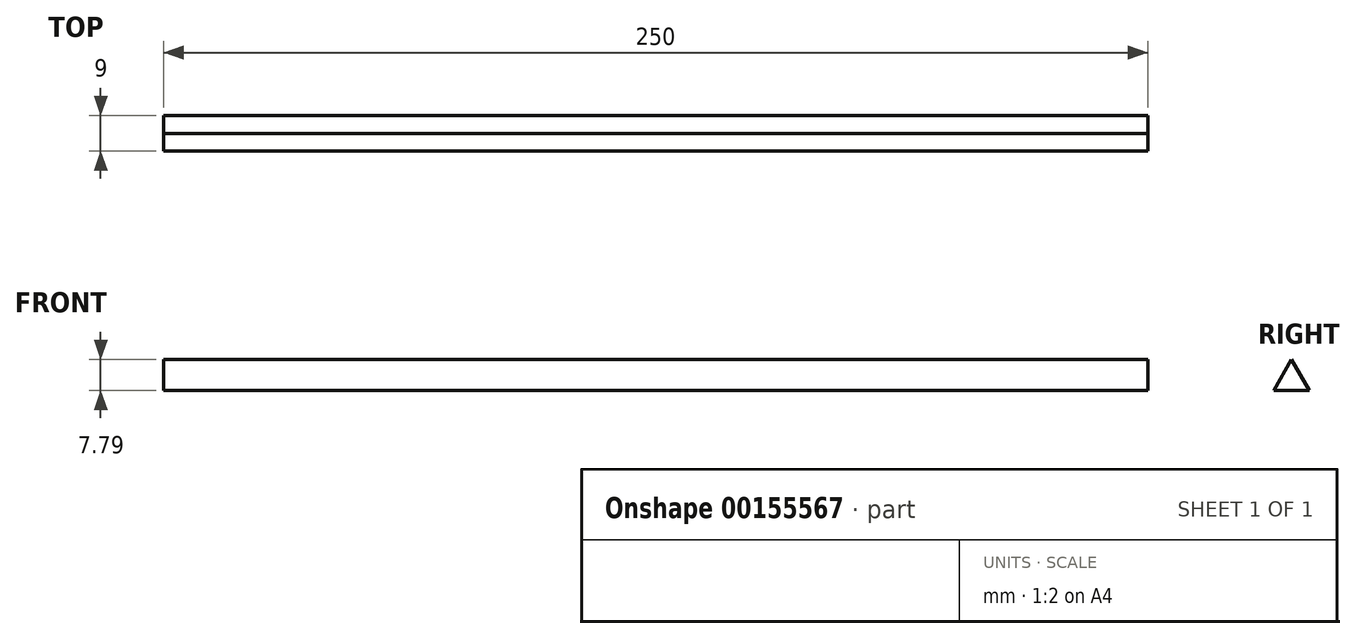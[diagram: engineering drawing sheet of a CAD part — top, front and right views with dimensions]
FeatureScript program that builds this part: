
annotation { "Feature Type Name" : "Feature", "Feature Type Description" : "" }
export const myFeature = defineFeature(function(context is Context, id is Id, definition is map)
    precondition{}
    {
        {
            var Q0;
            Q0=qCreatedBy(makeId("Right.planeOp"),FACE);
            var sketch = newSketch(context, id + "F0", { "sketchPlane" : qUnion([Q0])});
            skCircle(sketch, "E0.cCircle", {"center": v(0, 2.99) * mm, "radius": 2.6 * mm, "construction": true});
            skLineSegment(sketch, "E0.0", {"start": v(0, 8.18) * mm, "end": v(4.5, 0.39) * mm});
            skLineSegment(sketch, "E0.1", {"start": v(4.5, 0.39) * mm, "end": v(-4.5, 0.39) * mm});
            skLineSegment(sketch, "E0.2", {"start": v(-4.5, 0.39) * mm, "end": v(0, 8.18) * mm});
            skPoint(sketch, "E0.0.midPoint", {"position": v(2.25, 4.29) * mm});
            skSolve(sketch);
        }
        {
            var Q0;
            Q0=makeQuery(id+"F0.imprint","IMPRINT",FACE,{"disambiguationData":[TD([[makeQuery(id+"F0.imprint","IMPRINT",EDGE,{"derivedFrom":sQuery(id+"F0.wireOp",EDGE,"E0.0")}),-1.0]])]});
            extrude(context, id + "F1", {"entities" : qUnion([Q0]), "endBound" : BoundingType.SYMMETRIC, "depth" : 250 * mm});
        }
    });
